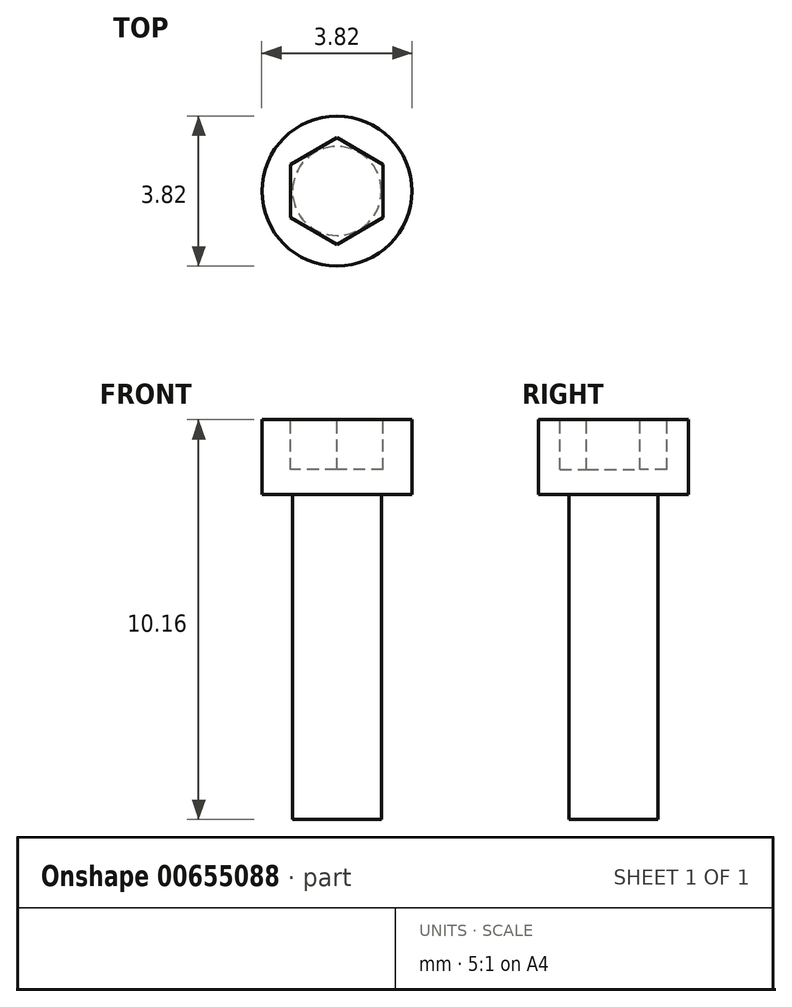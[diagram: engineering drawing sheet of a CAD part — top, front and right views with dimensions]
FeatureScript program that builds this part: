
annotation { "Feature Type Name" : "Feature", "Feature Type Description" : "" }
export const myFeature = defineFeature(function(context is Context, id is Id, definition is map)
    precondition{}
    {
        {
            var Q0;
            Q0=qCreatedBy(makeId("Front.planeOp"),FACE);
            var sketch = newSketch(context, id + "F0", { "sketchPlane" : qUnion([Q0])});
            skLineSegment(sketch, "E0", {"start": v(0, 2.35) * mm, "end": v(0, -7.8) * mm});
            skLineSegment(sketch, "E1", {"start": v(0, -7.8) * mm, "end": v(1.13, -7.8) * mm});
            skLineSegment(sketch, "E2", {"start": v(1.13, -7.8) * mm, "end": v(1.13, 0.45) * mm});
            skLineSegment(sketch, "E3", {"start": v(1.13, 0.45) * mm, "end": v(1.9, 0.45) * mm});
            skLineSegment(sketch, "E4", {"start": v(1.9, 0.45) * mm, "end": v(1.9, 2.35) * mm});
            skLineSegment(sketch, "E5", {"start": v(1.9, 2.35) * mm, "end": v(0, 2.35) * mm});
            skSolve(sketch);
        }
        {
            var Q0;
            Q0 = qSketchRegion(id + "F0", true);
            var Q1;
            Q1=sQuery(id+"F0.wireOp",EDGE,"E0");
            revolve(context, id + "F1", {"entities" : qUnion([Q0]), "axis" : qUnion([Q1]), "revolveType" : RevolveType.FULL});
        }
        {
            var Q0;
            Q0=makeQuery(id+"F1.opRevolve","SWEPT_FACE",FACE,{"disambiguationData":[OSD([sQuery(id+"F0.wireOp",EDGE,"E5")])]});
            var sketch = newSketch(context, id + "F2", { "sketchPlane" : qUnion([Q0])});
            skCircle(sketch, "E6.cCircle", {"center": v(0, 0) * mm, "radius": 1.18 * mm, "construction": true});
            skLineSegment(sketch, "E6.0", {"start": v(-1.18, -0.68) * mm, "end": v(-1.18, 0.68) * mm});
            skLineSegment(sketch, "E6.1", {"start": v(-1.18, 0.68) * mm, "end": v(0, 1.36) * mm});
            skLineSegment(sketch, "E6.2", {"start": v(0, 1.36) * mm, "end": v(1.18, 0.68) * mm});
            skLineSegment(sketch, "E6.3", {"start": v(1.18, 0.68) * mm, "end": v(1.18, -0.68) * mm});
            skLineSegment(sketch, "E6.4", {"start": v(1.18, -0.68) * mm, "end": v(0, -1.36) * mm});
            skLineSegment(sketch, "E6.5", {"start": v(0, -1.36) * mm, "end": v(-1.18, -0.68) * mm});
            skPoint(sketch, "E6.0.midPoint", {"position": v(-1.18, 0) * mm});
            skSolve(sketch);
        }
        {
            var Q0;
            Q0 = qSketchRegion(id + "F2", true);
            extrude(context, id + "F3", {"entities" : qUnion([Q0]), "operationType" : NewBodyOperationType.REMOVE, "oppositeDirection" : true, "depth" : 1.27 * mm, "offsetDistance" : 25.4 * mm});
        }
    });
